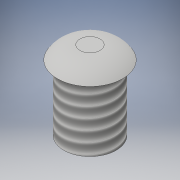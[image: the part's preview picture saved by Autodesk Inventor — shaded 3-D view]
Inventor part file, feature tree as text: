
AUTODESK INVENTOR PART (.ipt)
format: ipt  version: 2019.1 (Build 231200000, 200)  size: 126,976 bytes
history: native  units: in
note: dims shown in document units (in); Inventor stores cm internally (conversion verified against a paired STEP export)
features: extrude x2, sketch x2, thread x1, fillet x1
ambient origin geometry x8: Origin, YZ Plane, XZ Plane, XY Plane, X Axis, Y Axis, Z Axis, Center Point
bodies: Solid1 (feature_tree)
feature tree (6):
  extrude  "Extrusion1"  Depth=0.0984in TaperAngle=0.0deg
  thread  "Thread1"  [1 undecoded]
  extrude  "Extrusion2"  Depth=0.0197in TaperAngle=0.0deg
  fillet  "Fillet1"  Radius=0.0394in
  sketch  "Sketch1"  dims[d0=0.0787in d1=0.0984in d2=0.0in d3=0.3937in d4=0.0in]
  sketch  "Sketch2"  dims[d5=0.0984in d6=0.0197in d7=0.0in d8=0.0394in]
note: 1 required parameter value undecoded (feature->parameter linkage not recoverable at this tier; creation-order binding heuristic only, values carry confidence <= 0.55)
